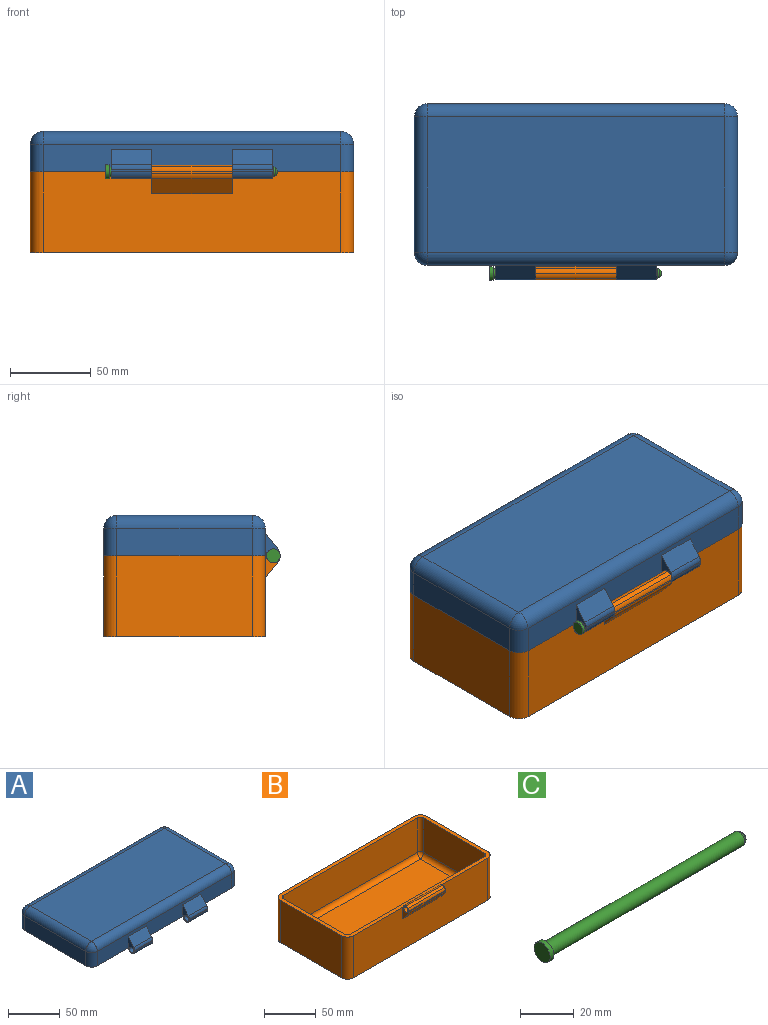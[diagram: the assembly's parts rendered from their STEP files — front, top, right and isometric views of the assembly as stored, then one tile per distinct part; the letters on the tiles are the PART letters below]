
ASSEMBLY  parts=3 mates=2
PART A: 59 faces, bbox 200x109x29 mm
  f0: plane 184x17mm, normal (0,-1,0), area 2541.4mm2, adj f1,f6,f8,f9,f36,f37,f40,f41
  f1: plane 200x100mm, normal (0,0,-1), area 2294.8mm2, adj f0,f2,f3,f4,f6,f8,f11,f17
  f2: plane 84x17mm, normal (1,0,0), area 1428mm2, adj f1,f8,f14,f17
  f3: plane 184x17mm, normal (0,1,0), area 3128mm2, adj f1,f11,f15,f17
  f4: plane 84x17mm, normal (-1,0,0), area 1428mm2, adj f1,f6,f10,f11
  f5: plane 184x84mm, normal (0,0,1), area 15456mm2, adj f9,f10,f14,f15
  f6: cylinder r=8mm len=17mm, axis (0,0,1), area 213.6mm2, adj f0,f1,f4,f7
  f7: sphere r=8mm, area 100.5mm2, adj f6,f9,f10
  f8: cylinder r=8mm len=17mm, axis (0,0,-1), area 213.6mm2, adj f0,f1,f2,f12
  f9: cylinder r=8mm len=184mm, axis (-1,0,0), area 2312.2mm2, adj f0,f5,f7,f12
  f10: cylinder r=8mm len=84mm, axis (0,1,0), area 1055.6mm2, adj f4,f5,f7,f13
  f11: cylinder r=8mm len=17mm, axis (0,0,-1), area 213.6mm2, adj f1,f3,f4,f13
  f12: sphere r=8mm, area 100.5mm2, adj f8,f9,f14
  f13: sphere r=8mm, area 100.5mm2, adj f10,f11,f15
  f14: cylinder r=8mm len=84mm, axis (0,-1,0), area 1055.6mm2, adj f2,f5,f12,f16
  f15: cylinder r=8mm len=184mm, axis (1,0,0), area 2312.2mm2, adj f3,f5,f13,f16
  f16: sphere r=8mm, area 100.5mm2, adj f14,f15,f17
  f17: cylinder r=8mm len=17mm, axis (0,0,1), area 213.6mm2, adj f1,f2,f3,f16
  f18: plane 84x17mm, normal (-1,0,0), area 1428mm2, adj f1,f25,f31,f34
  f19: plane 184x17mm, normal (0,-1,0), area 3128mm2, adj f1,f28,f32,f34
  f20: plane 84x17mm, normal (1,0,0), area 1428mm2, adj f1,f23,f27,f28
  f21: plane 184x17mm, normal (0,1,0), area 3128mm2, adj f1,f23,f25,f26
  f22: plane 184x84mm, normal (0,0,-1), area 15456mm2, adj f26,f27,f31,f32
  f23: cylinder r=4mm len=17mm, axis (0,0,1), area 106.8mm2, adj f1,f20,f21,f24
  f24: sphere r=4mm, area 25.1mm2, adj f23,f26,f27
  f25: cylinder r=4mm len=17mm, axis (0,0,-1), area 106.8mm2, adj f1,f18,f21,f29
  f26: cylinder r=4mm len=184mm, axis (-1,0,0), area 1156.1mm2, adj f21,f22,f24,f29
  f27: cylinder r=4mm len=84mm, axis (0,1,0), area 527.8mm2, adj f20,f22,f24,f30
  f28: cylinder r=4mm len=17mm, axis (0,0,-1), area 106.8mm2, adj f1,f19,f20,f30
  f29: sphere r=4mm, area 25.1mm2, adj f25,f26,f31
  f30: sphere r=4mm, area 25.1mm2, adj f27,f28,f32
  f31: cylinder r=4mm len=84mm, axis (0,-1,0), area 527.8mm2, adj f18,f22,f29,f33
  f32: cylinder r=4mm len=184mm, axis (1,0,0), area 1156.1mm2, adj f19,f22,f30,f33
  f33: sphere r=4mm, area 25.1mm2, adj f31,f32,f34
  f34: cylinder r=4mm len=17mm, axis (0,0,1), area 106.8mm2, adj f1,f18,f19,f33
  f35: plane 25x1.78mm, normal (0,1,0), area 44.4mm2, adj f36,f40,f41,f53
  f36: plane 25x1mm, normal (0,0,-1), area 25mm2, adj f0,f35,f40,f41
  f37: plane 25x9.33mm, normal (0,-0.77,0.64), area 304.5mm2, adj f0,f40,f41,f58
  f38: plane 25x0.96mm, normal (0,-1,0), area 24mm2, adj f40,f41,f56,f58
  f39: cylinder r=3mm len=25mm, axis (-1,0,0), area 471.2mm2, adj f40,f41
  f40: plane 17.65x9mm, normal (1,0,0), area 69.6mm2, adj f0,f35,f36,f37,f38,f39,f53,f54
  f41: plane 17.65x9mm, normal (-1,0,0), area 69.6mm2, adj f0,f35,f36,f37,f38,f39,f53,f54
  f42: plane 25x9.33mm, normal (0,-0.77,0.64), area 304.5mm2, adj f0,f47,f48,f57
  f43: plane 25x0.96mm, normal (0,-1,0), area 24mm2, adj f47,f48,f52,f57
  f44: plane 25x1.78mm, normal (0,1,0), area 44.4mm2, adj f46,f47,f48,f49
  f45: cylinder r=3mm len=25mm, axis (1,0,0), area 471.2mm2, adj f47,f48
  f46: plane 25x1mm, normal (0,0,-1), area 25mm2, adj f0,f44,f47,f48
  f47: plane 17.65x9mm, normal (-1,0,0), area 69.6mm2, adj f0,f42,f43,f44,f45,f46,f49,f50
  f48: plane 17.65x9mm, normal (1,0,0), area 69.6mm2, adj f0,f42,f43,f44,f45,f46,f49,f50
  f49: cylinder r=5mm len=25mm, axis (1,0,0), area 83mm2, adj f44,f47,f48,f50
  f50: cylinder r=5mm len=25mm, axis (1,0,0), area 79.4mm2, adj f47,f48,f49,f51
  f51: cylinder r=5mm len=25mm, axis (1,0,0), area 79.4mm2, adj f47,f48,f50,f52
  f52: cylinder r=5mm len=25mm, axis (1,0,0), area 83mm2, adj f43,f47,f48,f51
  f53: cylinder r=5mm len=25mm, axis (-1,0,0), area 83mm2, adj f35,f40,f41,f54
  f54: cylinder r=5mm len=25mm, axis (-1,0,0), area 79.4mm2, adj f40,f41,f53,f55
  f55: cylinder r=5mm len=25mm, axis (-1,0,0), area 79.4mm2, adj f40,f41,f54,f56
  f56: cylinder r=5mm len=25mm, axis (-1,0,0), area 83mm2, adj f38,f40,f41,f55
  f57: cylinder r=5mm len=25mm, axis (1,0,0), area 87.3mm2, adj f42,f43,f47,f48
  f58: cylinder r=5mm len=25mm, axis (-1,0,0), area 87.3mm2, adj f37,f38,f40,f41
PART B: 39 faces, bbox 200x109x54.1 mm
  f0: plane 200x100mm, normal (0,0,1), area 2294.8mm2, adj f2,f3,f4,f5,f6,f7,f8,f9
  f1: plane 200x100mm, normal (0,0,-1), area 19945.1mm2, adj f2,f3,f4,f5,f6,f7,f8,f9
  f2: cylinder r=8mm len=50mm, axis (0,0,1), area 628.3mm2, adj f0,f1,f4,f6
  f3: cylinder r=8mm len=50mm, axis (0,0,-1), area 628.3mm2, adj f0,f1,f4,f9
  f4: plane 184x50mm, normal (0,-1,0), area 8613.4mm2, adj f0,f1,f2,f3,f27,f28,f30,f31
  f5: cylinder r=8mm len=50mm, axis (0,0,-1), area 628.3mm2, adj f0,f1,f6,f8
  f6: plane 84x50mm, normal (-1,0,0), area 4200mm2, adj f0,f1,f2,f5
  f7: cylinder r=8mm len=50mm, axis (0,0,1), area 628.3mm2, adj f0,f1,f8,f9
  f8: plane 184x50mm, normal (0,1,0), area 9200mm2, adj f0,f1,f5,f7
  f9: plane 84x50mm, normal (1,0,0), area 4200mm2, adj f0,f1,f3,f7
  f10: plane 182x82mm, normal (0,0,1), area 14924mm2, adj f19,f22,f23,f26
  f11: cylinder r=4mm len=41mm, axis (0,0,1), area 257.6mm2, adj f0,f13,f15,f21
  f12: cylinder r=4mm len=41mm, axis (0,0,-1), area 257.6mm2, adj f0,f13,f18,f20
  f13: plane 184x41mm, normal (0,1,0), area 7544mm2, adj f0,f11,f12,f19
  f14: cylinder r=4mm len=41mm, axis (0,0,-1), area 257.6mm2, adj f0,f15,f17,f25
  f15: plane 84x41mm, normal (1,0,0), area 3444mm2, adj f0,f11,f14,f23
  f16: cylinder r=4mm len=41mm, axis (0,0,1), area 257.6mm2, adj f0,f17,f18,f24
  f17: plane 184x41mm, normal (0,-1,0), area 7544mm2, adj f0,f14,f16,f26
  f18: plane 84x41mm, normal (-1,0,0), area 3444mm2, adj f0,f12,f16,f22
  f19: cylinder r=5mm len=184mm, axis (-1,0,0), area 1439.4mm2, adj f10,f13,f20,f21
  f20: bspline ~6.16x5mm, area 32.1mm2, adj f12,f19,f22
  f21: bspline ~6.16x5mm, area 32.1mm2, adj f11,f19,f23
  f22: cylinder r=5mm len=84mm, axis (0,-1,0), area 654mm2, adj f10,f18,f20,f24
  f23: cylinder r=5mm len=84mm, axis (0,1,0), area 654mm2, adj f10,f15,f21,f25
  f24: bspline ~6.16x5mm, area 32.1mm2, adj f16,f22,f26
  f25: bspline ~6.16x5mm, area 32.1mm2, adj f14,f23,f26
  f26: cylinder r=5mm len=184mm, axis (1,0,0), area 1439.4mm2, adj f10,f17,f24,f25
  f27: plane 17.65x9mm, normal (1,0,0), area 69.6mm2, adj f4,f28,f29,f31,f32,f33,f34,f35
  f28: plane 50x1mm, normal (0,0,1), area 50mm2, adj f4,f27,f29,f30
  f29: plane 50x1.78mm, normal (0,1,0), area 88.8mm2, adj f27,f28,f30,f37
  f30: plane 17.65x9mm, normal (-1,0,0), area 69.6mm2, adj f4,f28,f29,f31,f32,f33,f34,f35
  f31: plane 50x9.33mm, normal (0,-0.77,-0.64), area 609.1mm2, adj f4,f27,f30,f38
  f32: plane 50x0.96mm, normal (0,-1,0), area 48mm2, adj f27,f30,f34,f38
  f33: cylinder r=3mm len=50mm, axis (-1,0,0), area 942.5mm2, adj f27,f30
  f34: cylinder r=5mm len=50mm, axis (-1,0,0), area 166mm2, adj f27,f30,f32,f35
  f35: cylinder r=5mm len=50mm, axis (-1,0,0), area 158.8mm2, adj f27,f30,f34,f36
  f36: cylinder r=5mm len=50mm, axis (-1,0,0), area 158.8mm2, adj f27,f30,f35,f37
  f37: cylinder r=5mm len=50mm, axis (-1,0,0), area 166mm2, adj f27,f29,f30,f36
  f38: cylinder r=5mm len=50mm, axis (-1,0,0), area 174.5mm2, adj f27,f30,f31,f32
PART C: 7 faces, bbox 106x8.5x8.5 mm
  f0: cylinder r=3mm len=102mm, axis (1,0,0), area 1922.7mm2, adj f4,f5
  f1: plane 1.53x1.53mm, normal (1,0,0), area 1.8mm2, adj f6
  f2: cylinder r=4.25mm len=8.5mm, axis (1,0,0), area 53.4mm2, adj f3,f4
  f3: plane 8.5x8.5mm, normal (-1,0,0), area 56.7mm2, adj f2
  f4: plane 8.5x8.5mm, normal (1,0,0), area 28.5mm2, adj f0,f2
  f5: cone r=3mm half-angle=26.6deg, axis (-1,0,0), area 17.4mm2, adj f0,f6
  f6: torus R=0.76mm, axis (-1,0,0), area 24.5mm2, adj f1,f5
PLACE A rot(axis=(1,0,0),0deg) t=(13.96,17.72,-19.29)mm
PLACE B t=(13.96,17.72,-19.29)mm fixed
PLACE C t=(14.61,17.72,-19.29)mm
MATE revolute B.f33 <-> A.f39  axis (-1,0,0) through (38.96,-37.28,30.71)mm
MATE slider C.f0 <-> B.f33  axis (1,0,0) through (13.61,-37.28,30.71)mm
